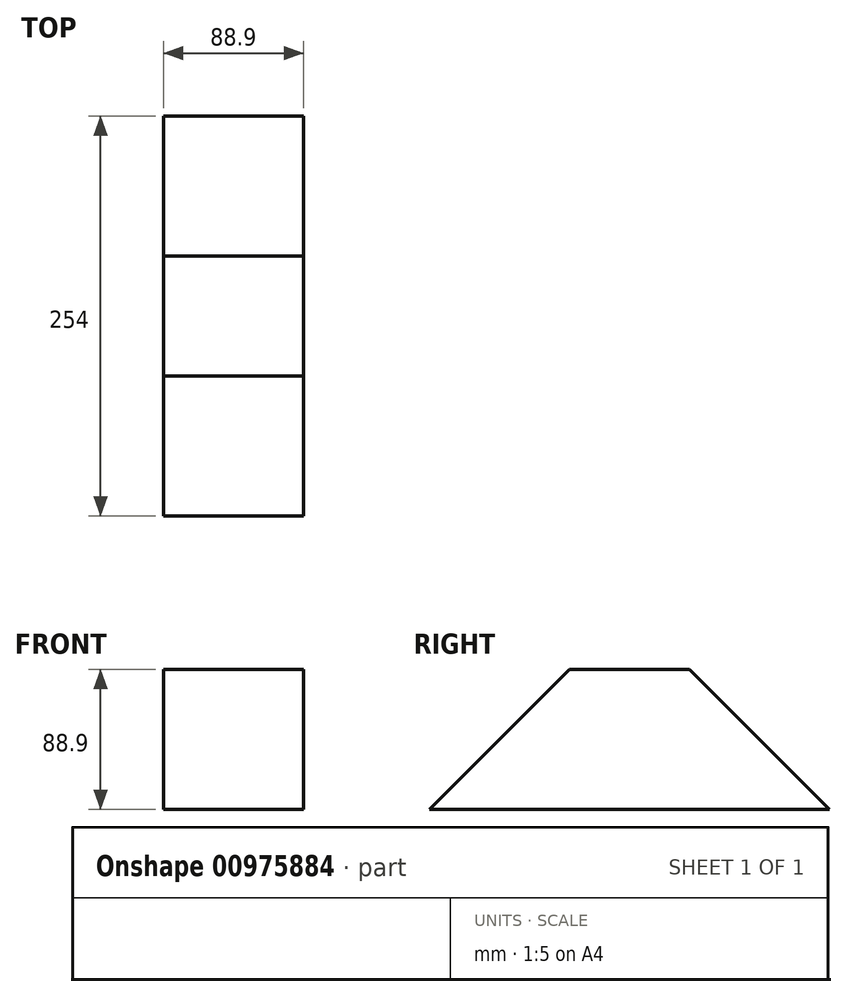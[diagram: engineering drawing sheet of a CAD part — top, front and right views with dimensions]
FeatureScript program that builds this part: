
annotation { "Feature Type Name" : "Feature", "Feature Type Description" : "" }
export const myFeature = defineFeature(function(context is Context, id is Id, definition is map)
    precondition{}
    {
        {
            var Q0;
            Q0=qCreatedBy(makeId("Right.planeOp"),FACE);
            var sketch = newSketch(context, id + "F0", { "sketchPlane" : qUnion([Q0])});
            skLineSegment(sketch, "E0.bottom", {"start": v(0, 0) * mm, "end": v(0, 0) * mm});
            skLineSegment(sketch, "E0.top", {"start": v(0, 0) * mm, "end": v(0, 0) * mm});
            skLineSegment(sketch, "E0.left", {"start": v(0, 0) * mm, "end": v(0, 0) * mm});
            skLineSegment(sketch, "E0.right", {"start": v(0, 0) * mm, "end": v(0, 0) * mm});
            skPoint(sketch, "E0.middle", {"position": v(0, 0) * mm});
            skLineSegment(sketch, "E1.bottom", {"start": v(0, 44.45) * mm, "end": v(-38.1, 44.45) * mm});
            skLineSegment(sketch, "E1.top", {"start": v(0, -44.45) * mm, "end": v(-127, -44.45) * mm});
            skLineSegment(sketch, "E2", {"start": v(-127, -44.45) * mm, "end": v(-38.1, 44.45) * mm});
            skPoint(sketch, "E3.orphan", {"position": v(-127, 44.45) * mm});
            skPoint(sketch, "E1.left.end.orphan", {"position": v(127, -44.45) * mm});
            skPoint(sketch, "E1.left.start.orphan", {"position": v(127, 44.45) * mm});
            skLineSegment(sketch, "E4.MirrorCS", {"start": v(0, -44.45) * mm, "end": v(127, -44.45) * mm});
            skLineSegment(sketch, "E5.MirrorCS", {"start": v(127, -44.45) * mm, "end": v(38.1, 44.45) * mm});
            skLineSegment(sketch, "E6.MirrorCS", {"start": v(0, 44.45) * mm, "end": v(38.1, 44.45) * mm});
            skSolve(sketch);
        }
        {
            var Q0;
            Q0=qSketchRegion(id+"F0",true);
            extrude(context, id + "F1", {"entities" : qUnion([Q0]), "depth" : 88.9 * mm, "offsetDistance" : 25.4 * mm});
        }
    });
